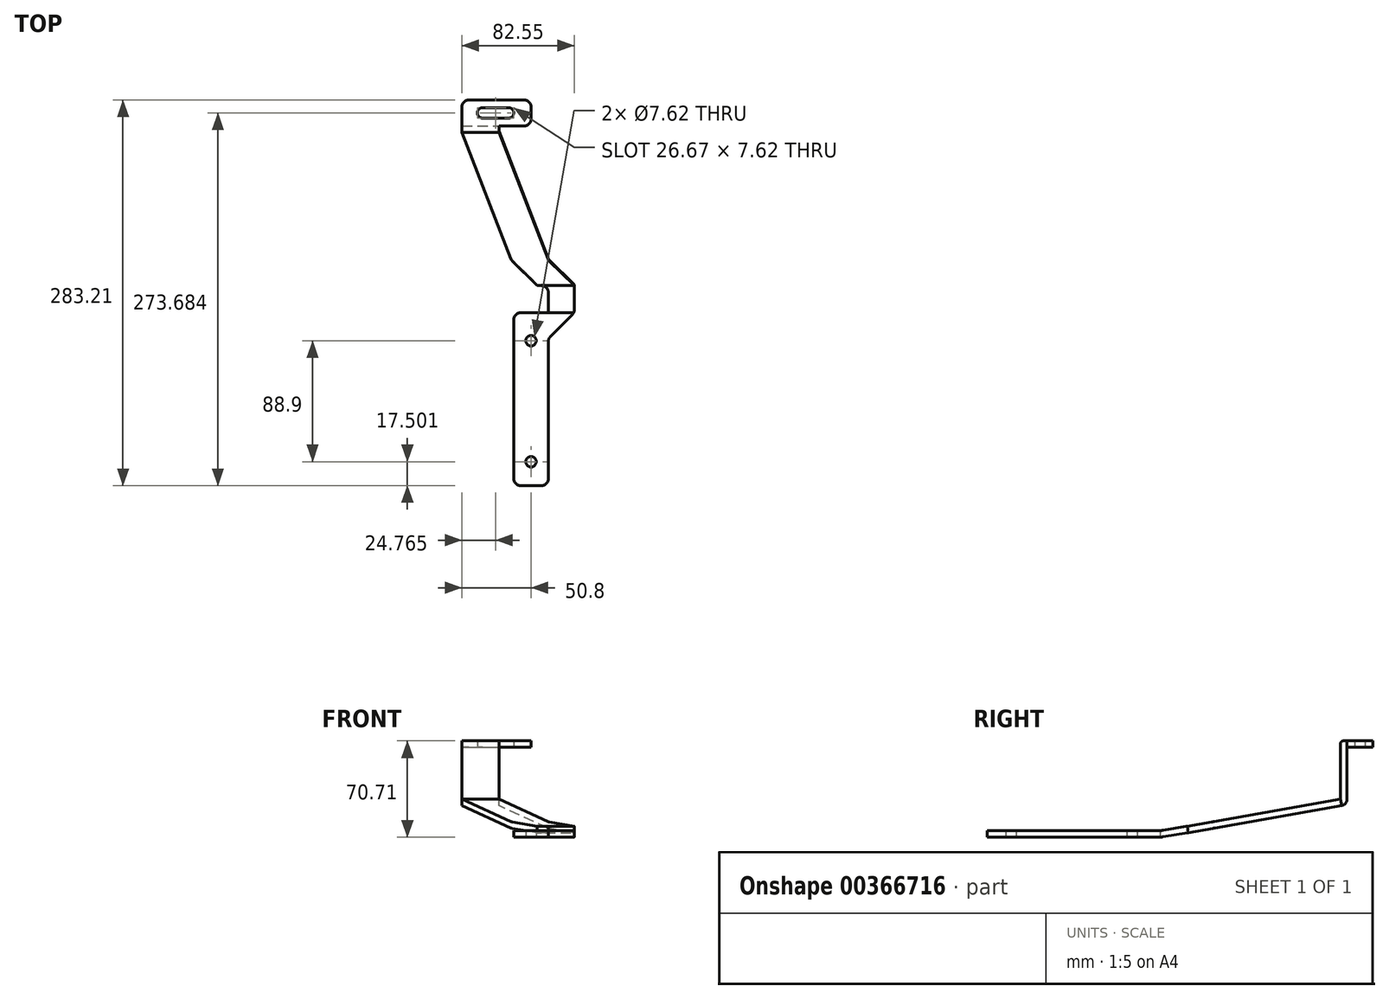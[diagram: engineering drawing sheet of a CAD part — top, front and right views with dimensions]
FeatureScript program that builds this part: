
annotation { "Feature Type Name" : "Feature", "Feature Type Description" : "" }
export const myFeature = defineFeature(function(context is Context, id is Id, definition is map)
    precondition{}
    {
        {
            var Q0;
            Q0=qCreatedBy(makeId("Top.planeOp"),FACE);
            var sketch = newSketch(context, id + "F0", { "sketchPlane" : qUnion([Q0])});
            skLineSegment(sketch, "E0.bottom", {"start": v(5.08, 0) * mm, "end": v(20.32, 0) * mm});
            skLineSegment(sketch, "E0.top", {"start": v(5.08, 127) * mm, "end": v(25.4, 127) * mm});
            skLineSegment(sketch, "E0.left", {"start": v(0, 5.08) * mm, "end": v(0, 121.92) * mm});
            skLineSegment(sketch, "E0.right", {"start": v(25.4, 5.08) * mm, "end": v(25.4, 105.85) * mm});
            skCircle(sketch, "E1", {"center": v(12.7, 17.5) * mm, "radius": 3.81 * mm});
            skCircle(sketch, "E2", {"center": v(12.7, 106.4) * mm, "radius": 3.81 * mm});
            skLineSegment(sketch, "E3", {"start": v(12.7, 127) * mm, "end": v(12.7, 0) * mm, "construction": true});
            skLineSegment(sketch, "E4", {"start": v(25.4, 127) * mm, "end": v(44.45, 127) * mm});
            skLineSegment(sketch, "E5", {"start": v(44.45, 127) * mm, "end": v(26.89, 109.44) * mm});
            skPoint(sketch, "E6.visualSharp", {"position": v(0, 127) * mm});
            skArc(sketch, "E6.filletArc", {"start": v(5.08, 127) * mm, "mid": v(1.49, 125.51) * mm, "end": v(0, 121.92) * mm});
            skPoint(sketch, "E7.visualSharp", {"position": v(0, 0) * mm});
            skArc(sketch, "E7.filletArc", {"start": v(0, 5.08) * mm, "mid": v(1.49, 1.49) * mm, "end": v(5.08, 0) * mm});
            skPoint(sketch, "E8.visualSharp", {"position": v(25.4, 0) * mm});
            skArc(sketch, "E8.filletArc", {"start": v(20.32, 0) * mm, "mid": v(23.91, 1.49) * mm, "end": v(25.4, 5.08) * mm});
            skPoint(sketch, "E9.visualSharp", {"position": v(25.4, 107.95) * mm});
            skArc(sketch, "E9.filletArc", {"start": v(26.89, 109.44) * mm, "mid": v(25.79, 107.79) * mm, "end": v(25.4, 105.85) * mm});
            skSolve(sketch);
        }
        {
            var Q0;
            Q0 = qSketchRegion(id + "F0", true);
            extrude(context, id + "F1", {"entities" : qUnion([Q0]), "depth" : 4.76 * mm});
        }
        {
            var Q0;
            Q0=qCreatedBy(makeId("Right.planeOp"),FACE);
            cPlane(context, id + "F2", {"entities" : qUnion([Q0]), "cplaneType" : CPlaneType.OFFSET, "offset" : 44.45 * mm, "width" : 152.4 * mm, "height" : 152.4 * mm});
        }
        {
            var Q0;
            Q0=qCreatedBy(id+"F2.planeOp",FACE);
            var sketch = newSketch(context, id + "F3", { "sketchPlane" : qUnion([Q0])});
            skLineSegment(sketch, "E10", {"start": v(127, 4.76) * mm, "end": v(146.05, 7.94) * mm});
            skLineSegment(sketch, "E11", {"start": v(146.05, 7.94) * mm, "end": v(146.83, 3.24) * mm, "construction": true});
            skLineSegment(sketch, "E12", {"start": v(127, 4.76) * mm, "end": v(127, 0) * mm});
            skLineSegment(sketch, "E13", {"start": v(146.83, 3.24) * mm, "end": v(146.83, 8) * mm});
            skArc(sketch, "E14", {"start": v(146.83, 8) * mm, "mid": v(146.44, 7.99) * mm, "end": v(146.05, 7.94) * mm});
            skArc(sketch, "E15", {"start": v(127, 0) * mm, "mid": v(127.42, 0.02) * mm, "end": v(127.83, 0.07) * mm});
            skLineSegment(sketch, "E16", {"start": v(127, 4.76) * mm, "end": v(127.83, 0.07) * mm, "construction": true});
            skLineSegment(sketch, "E17", {"start": v(127.83, 0.07) * mm, "end": v(146.83, 3.24) * mm});
            skSolve(sketch);
        }
        {
            var Q0;
            Q0 = qSketchRegion(id + "F3", true);
            extrude(context, id + "F4", {"entities" : qUnion([Q0]), "operationType" : NewBodyOperationType.ADD, "oppositeDirection" : true, "depth" : 19.05 * mm});
        }
        {
            var Q0;
            Q0=makeQuery(id+"F4.opExtrude","CAP_FACE",FACE,{"disambiguationData":[OSD([sQuery(id+"F3.wireOp",EDGE,"E10"),sQuery(id+"F3.wireOp",EDGE,"E12"),sQuery(id+"F3.wireOp",EDGE,"E13"),sQuery(id+"F3.wireOp",EDGE,"E14"),sQuery(id+"F3.wireOp",EDGE,"E15"),sQuery(id+"F3.wireOp",EDGE,"E17")])],"isStart":true});
            var sketch = newSketch(context, id + "F5", { "sketchPlane" : qUnion([Q0])});
            skArc(sketch, "E18", {"start": v(146.83, 3.24) * mm, "mid": v(147.25, 3.26) * mm, "end": v(147.66, 3.31) * mm});
            skLineSegment(sketch, "E19", {"start": v(146.83, 8) * mm, "end": v(147.66, 3.31) * mm});
            skLineSegment(sketch, "E20", {"start": v(146.83, 8) * mm, "end": v(146.83, 3.24) * mm});
            skLineSegment(sketch, "E21", {"start": v(146.83, 8) * mm, "end": v(259.4, 27.85) * mm});
            skLineSegment(sketch, "E22", {"start": v(259.4, 27.85) * mm, "end": v(260.22, 23.16) * mm});
            skLineSegment(sketch, "E23", {"start": v(260.22, 23.16) * mm, "end": v(147.66, 3.31) * mm});
            skSolve(sketch);
        }
        {
            var Q0;
            Q0 = qSketchRegion(id + "F5", true);
            extrude(context, id + "F6", {"entities" : qUnion([Q0]), "operationType" : NewBodyOperationType.ADD, "oppositeDirection" : true, "depth" : 105.92 * mm});
        }
        {
            var Q0;
            Q0=makeQuery(id+"F6.opExtrude","SWEPT_FACE",FACE,{"disambiguationData":[OSD([sQuery(id+"F5.wireOp",EDGE,"E21")])]});
            var sketch = newSketch(context, id + "F7", { "sketchPlane" : qUnion([Q0])});
            skLineSegment(sketch, "E24", {"start": v(44.45, 146) * mm, "end": v(25.4, 165.04) * mm});
            skLineSegment(sketch, "E25", {"start": v(25.4, 165.04) * mm, "end": v(25.4, 146) * mm, "construction": true});
            skLineSegment(sketch, "E26", {"start": v(-38.1, 146) * mm, "end": v(-38.1, 260.3) * mm, "construction": true});
            skLineSegment(sketch, "E27", {"start": v(17.27, 146) * mm, "end": v(-1.78, 165.04) * mm});
            skLineSegment(sketch, "E28", {"start": v(25.4, 165.04) * mm, "end": v(-1.78, 165.04) * mm, "construction": true});
            skLineSegment(sketch, "E29", {"start": v(-1.78, 165.04) * mm, "end": v(-38.1, 260.3) * mm});
            skLineSegment(sketch, "E30", {"start": v(25.4, 165.04) * mm, "end": v(-10.92, 260.3) * mm});
            skLineSegment(sketch, "E31", {"start": v(-38.1, 260.3) * mm, "end": v(-61.47, 260.3) * mm});
            skLineSegment(sketch, "E32", {"start": v(-61.47, 260.3) * mm, "end": v(-61.47, 146) * mm});
            skLineSegment(sketch, "E33", {"start": v(44.45, 146) * mm, "end": v(44.45, 260.3) * mm});
            skLineSegment(sketch, "E34", {"start": v(44.45, 260.3) * mm, "end": v(-10.92, 260.3) * mm});
            skLineSegment(sketch, "E35", {"start": v(-61.47, 146) * mm, "end": v(-61.47, 141.6) * mm});
            skLineSegment(sketch, "E36", {"start": v(-61.47, 141.6) * mm, "end": v(18.9, 141.6) * mm});
            skLineSegment(sketch, "E37", {"start": v(18.9, 141.6) * mm, "end": v(17.27, 146) * mm});
            skSolve(sketch);
        }
        {
            var Q0;
            Q0 = qSketchRegion(id + "F7", true);
            extrude(context, id + "F8", {"entities" : qUnion([Q0]), "operationType" : NewBodyOperationType.REMOVE, "oppositeDirection" : true, "depth" : 25.4 * mm});
        }
        {
            var Q0;
            Q0=qCreatedBy(makeId("Right.planeOp"),FACE);
            var sketch = newSketch(context, id + "F9", { "sketchPlane" : qUnion([Q0])});
            skArc(sketch, "E38", {"start": v(260.22, 23.16) * mm, "mid": v(263.04, 24.79) * mm, "end": v(264.16, 27.85) * mm});
            skLineSegment(sketch, "E39", {"start": v(259.4, 27.85) * mm, "end": v(259.4, 65.95) * mm});
            skLineSegment(sketch, "E40", {"start": v(259.4, 65.95) * mm, "end": v(264.16, 65.95) * mm});
            skLineSegment(sketch, "E41", {"start": v(264.16, 65.95) * mm, "end": v(264.16, 27.85) * mm});
            skLineSegment(sketch, "E42", {"start": v(259.4, 27.85) * mm, "end": v(260.22, 23.16) * mm});
            skSolve(sketch);
        }
        {
            var Q0;
            Q0 = qSketchRegion(id + "F9", true);
            var Q1;
            Q1=makeQuery(id+"F8.boolean.opBoolean","COPY",VERTEX,{"derivedFrom":makeQuery(id+"F8.opExtrude","CAP_VERTEX",VERTEX,{"disambiguationData":[OSD([sQuery(id+"F5.wireOp",EDGE,"E21"),sQuery(id+"F5.wireOp",EDGE,"E22"),sQuery(id+"F7.wireOp",EDGE,"E29"),sQuery(id+"F7.wireOp",EDGE,"E31")])],"isStart":true})});
            extrude(context, id + "F10", {"entities" : qUnion([Q0]), "operationType" : NewBodyOperationType.ADD, "endBound" : BoundingType.UP_TO_VERTEX, "oppositeDirection" : true, "endBoundEntityVertex" : qUnion([Q1]), "depth" : 25.4 * mm});
        }
        {
            var Q0;
            Q0=makeQuery(id+"F10.opExtrude","SWEPT_FACE",FACE,{"disambiguationData":[OSD([sQuery(id+"F9.wireOp",EDGE,"E42")])]});
            var sketch = newSketch(context, id + "F11", { "sketchPlane" : qUnion([Q0])});
            skLineSegment(sketch, "E43.bottom", {"start": v(-10.92, -22.38) * mm, "end": v(13.46, -22.38) * mm});
            skLineSegment(sketch, "E43.top", {"start": v(-10.92, 31.38) * mm, "end": v(13.46, 31.38) * mm});
            skLineSegment(sketch, "E43.left", {"start": v(-10.92, -22.38) * mm, "end": v(-10.92, 31.38) * mm});
            skLineSegment(sketch, "E43.right", {"start": v(13.46, -22.38) * mm, "end": v(13.46, 31.38) * mm});
            skSolve(sketch);
        }
        {
            var Q0;
            Q0 = qSketchRegion(id + "F11", true);
            extrude(context, id + "F12", {"entities" : qUnion([Q0]), "operationType" : NewBodyOperationType.REMOVE, "oppositeDirection" : true, "depth" : 25.4 * mm});
        }
        {
            var Q0;
            Q0=makeQuery(id+"F10.opExtrude","SWEPT_FACE",FACE,{"disambiguationData":[OSD([sQuery(id+"F9.wireOp",EDGE,"E40")])]});
            var sketch = newSketch(context, id + "F13", { "sketchPlane" : qUnion([Q0])});
            skLineSegment(sketch, "E44.bottom", {"start": v(-38.1, 259.4) * mm, "end": v(-10.92, 259.4) * mm});
            skLineSegment(sketch, "E44.top", {"start": v(-33.02, 283.2) * mm, "end": v(7.62, 283.2) * mm});
            skLineSegment(sketch, "E44.left", {"start": v(-38.1, 259.4) * mm, "end": v(-38.1, 278.13) * mm});
            skLineSegment(sketch, "E44.right", {"start": v(12.7, 269.24) * mm, "end": v(12.7, 278.13) * mm});
            skLineSegment(sketch, "E45", {"start": v(-10.92, 259.4) * mm, "end": v(-10.92, 264.16) * mm});
            skLineSegment(sketch, "E46", {"start": v(-10.92, 264.16) * mm, "end": v(7.62, 264.16) * mm});
            skLineSegment(sketch, "E47", {"start": v(-22.86, 273.68) * mm, "end": v(-3.81, 273.68) * mm});
            skArc(sketch, "E48.0.startCap", {"start": v(-22.86, 269.87) * mm, "mid": v(-26.67, 273.68) * mm, "end": v(-22.86, 277.5) * mm});
            skArc(sketch, "E48.0.endCap", {"start": v(-3.81, 277.5) * mm, "mid": v(0, 273.68) * mm, "end": v(-3.81, 269.87) * mm});
            skLineSegment(sketch, "E48.0.left", {"start": v(-22.86, 277.5) * mm, "end": v(-3.81, 277.5) * mm});
            skLineSegment(sketch, "E48.0.right", {"start": v(-22.86, 269.87) * mm, "end": v(-3.81, 269.87) * mm});
            skPoint(sketch, "E49.visualSharp", {"position": v(-38.1, 283.2) * mm});
            skArc(sketch, "E49.filletArc", {"start": v(-33.02, 283.2) * mm, "mid": v(-36.61, 281.72) * mm, "end": v(-38.1, 278.13) * mm});
            skPoint(sketch, "E50.visualSharp", {"position": v(12.7, 283.2) * mm});
            skArc(sketch, "E50.filletArc", {"start": v(12.7, 278.13) * mm, "mid": v(11.21, 281.72) * mm, "end": v(7.62, 283.2) * mm});
            skPoint(sketch, "E51.visualSharp", {"position": v(12.7, 264.16) * mm});
            skArc(sketch, "E51.filletArc", {"start": v(7.62, 264.16) * mm, "mid": v(11.21, 265.65) * mm, "end": v(12.7, 269.24) * mm});
            skSolve(sketch);
        }
        {
            var Q0;
            Q0 = qSketchRegion(id + "F13", true);
            extrude(context, id + "F14", {"entities" : qUnion([Q0]), "operationType" : NewBodyOperationType.ADD, "depth" : 4.76 * mm});
        }
        {
            var Q0;
            Q0=makeQuery(id+"F14.opExtrude","CAP_EDGE",EDGE,{"disambiguationData":[OSD([sQuery(id+"F13.wireOp",EDGE,"E44.bottom")])],"isStart":false});
            fillet(context, id + "F15", {"entities" : qUnion([Q0]), "radius" : 2.03 * mm, "tangentPropagation" : true, "allowEdgeOverflow" : false});
        }
        {
            var Q0;
            Q0=makeQuery(id+"F4.opExtrude","CAP_FACE",FACE,{"disambiguationData":[OSD([sQuery(id+"F3.wireOp",EDGE,"E10"),sQuery(id+"F3.wireOp",EDGE,"E12"),sQuery(id+"F3.wireOp",EDGE,"E13"),sQuery(id+"F3.wireOp",EDGE,"E14"),sQuery(id+"F3.wireOp",EDGE,"E15"),sQuery(id+"F3.wireOp",EDGE,"E17")])],"isStart":false});
            var sketch = newSketch(context, id + "F16", { "sketchPlane" : qUnion([Q0])});
            skLineSegment(sketch, "E52", {"start": v(-146.83, 8) * mm, "end": v(-146.83, 3.24) * mm});
            skLineSegment(sketch, "E53", {"start": v(-146.83, 8) * mm, "end": v(-147.66, 3.31) * mm});
            skArc(sketch, "E54", {"start": v(-147.66, 3.31) * mm, "mid": v(-147.25, 3.26) * mm, "end": v(-146.83, 3.24) * mm});
            skSolve(sketch);
        }
        {
            var Q0;
            Q0 = qSketchRegion(id + "F16", true);
            extrude(context, id + "F17", {"entities" : qUnion([Q0]), "operationType" : NewBodyOperationType.REMOVE, "depth" : 25.4 * mm});
        }
        {
            var Q0;
            Q0=makeQuery(id+"F8.boolean.opBoolean","COPY",EDGE,{"derivedFrom":makeQuery(id+"F8.opExtrude","SWEPT_EDGE",EDGE,{"disambiguationData":[OSD([sQuery(id+"F3.wireOp",EDGE,"E13"),sQuery(id+"F3.wireOp",EDGE,"E14"),sQuery(id+"F5.wireOp",EDGE,"E19"),sQuery(id+"F5.wireOp",EDGE,"E20"),sQuery(id+"F5.wireOp",EDGE,"E21"),sQuery(id+"F7.wireOp",EDGE,"E24"),sQuery(id+"F7.wireOp",EDGE,"E33")])]})});
            var Q1;
            Q1=makeQuery(id+"F4.boolean.opBoolean","MERGE",EDGE,{"derivedFrom":[makeQuery(id+"F1.opExtrude","SWEPT_EDGE",EDGE,{"disambiguationData":[OSD([sQuery(id+"F0.wireOp",EDGE,"E4"),sQuery(id+"F0.wireOp",EDGE,"E5")])]}),makeQuery(id+"F4.opExtrude","CAP_EDGE",EDGE,{"disambiguationData":[OSD([sQuery(id+"F3.wireOp",EDGE,"E12")])],"isStart":true})]});
            var Q2;
            Q2=makeQuery(id+"F4.opExtrude","CAP_EDGE",EDGE,{"disambiguationData":[OSD([sQuery(id+"F3.wireOp",EDGE,"E12")])],"isStart":false});
            var Q3;
            Q3=makeQuery(id+"F17.boolean.opBoolean","COPY",EDGE,{"derivedFrom":makeQuery(id+"F17.opExtrude","CAP_EDGE",EDGE,{"disambiguationData":[OSD([sQuery(id+"F16.wireOp",EDGE,"E53")])],"isStart":true})});
            var Q4;
            Q4=makeQuery(id+"F8.boolean.opBoolean","COPY",EDGE,{"derivedFrom":makeQuery(id+"F8.opExtrude","SWEPT_EDGE",EDGE,{"disambiguationData":[OSD([sQuery(id+"F3.wireOp",EDGE,"E14"),sQuery(id+"F5.wireOp",EDGE,"E19"),sQuery(id+"F5.wireOp",EDGE,"E20"),sQuery(id+"F5.wireOp",EDGE,"E21"),sQuery(id+"F7.wireOp",EDGE,"E27"),sQuery(id+"F7.wireOp",EDGE,"E37")])]})});
            var Q5;
            Q5=makeQuery(id+"F8.boolean.opBoolean","COPY",EDGE,{"derivedFrom":makeQuery(id+"F8.opExtrude","SWEPT_EDGE",EDGE,{"disambiguationData":[OSD([sQuery(id+"F7.wireOp",EDGE,"E27"),sQuery(id+"F7.wireOp",EDGE,"E29")])]})});
            var Q6;
            Q6=makeQuery(id+"F8.boolean.opBoolean","COPY",EDGE,{"derivedFrom":makeQuery(id+"F8.opExtrude","SWEPT_EDGE",EDGE,{"disambiguationData":[OSD([sQuery(id+"F7.wireOp",EDGE,"E24"),sQuery(id+"F7.wireOp",EDGE,"E30")])]})});
            fillet(context, id + "F18", {"entities" : qUnion([Q0, Q1, Q2, Q3, Q4, Q5, Q6]), "radius" : 5.08 * mm, "tangentPropagation" : true, "allowEdgeOverflow" : false});
        }
    });
